# Revit family: Haworth_Masters_Convergent_PTop
name_source: partatom
category: Furniture Systems
revit_build: Autodesk Revit 2018 (Build: 20170223_1515(x64)
units: mm (PartAtom-declared; Revit-internal decimal feet)

## family parameters
Always vertical = Yes
Cut with Voids When Loaded = No
OmniClass Number = 23.40.70.14.64.21
OmniClass Title = Systems Furniture
Part Type = Normal
Room Calculation Point = No
Round Connector Dimension = Use Diameter
Shared = No
Work Plane-Based = No

## types (4) — shared parameters
Actual Height = 29 1/8"
Actual Width = 72"
Assembly Code = E2020200
Cabinet Finish = Haworth _ Wood _ White Oak
Column Support = Yes
Custom Size = No
Description = Haworth - Masters - Convergent P-Top
Edge Finish = Haworth _ Wood _ White Oak
Manufacturer = Haworth
Model = Haworth - Masters - Convergent P-Top
One High = No
Post Finish = Haworth _ Paint _ Metallic Champagne
Revision Number = 2
Size = Verify Final Dim. w/ Haworth
Standard Depths = 30, 36 in.
Standard Widths = 54,60,66,72,78,84,90,96 in.
Support Height = 0"
Sustainability Info = http://www.haworth.com
Two High = Yes
URL = www.haworth.com
URL - Product = http://www.haworth.com
Warranty = http://www.haworth.com
Width = 72"
Worksurface Finish = Haworth _ Wood _ White Oak

## per-type parameters (varying)
| type | Actual Depth | Custom 30 | Custom 36 | Depth 30 | Depth 36 | Max. Width | Min. Width | Post Position | Support Position | T-Support |
| 36d 72w P-Top Attached | 36" | No | Yes | No | Yes | 96" | 66" | 24" | 18" | No |
| 36d 72w P-Top Desk | 36" | No | Yes | No | Yes | 96" | 66" | 24" | 18" | Yes |
| 30d 72w P-Top Attached | 30" | Yes | No | Yes | No | 90" | 54" | 21" | 15" | No |
| 30d 72w P-Top Desk | 30" | Yes | No | Yes | No | 90" | 54" | 21" | 15" | Yes |

## geometry (parser evidence)
native form markers: Sweep x5
no freeform markers — native parametric forms only
